# Revit family: 100800002 - Premier with base cabinets
name_source: partatom
category: Mechanical Equipment
units: mm (PartAtom-declared; Revit-internal decimal feet)

## family parameters
Always vertical = Yes
Cut with Voids When Loaded = No
Part Type = Normal
Room Calculation Point = No
Round Connector Dimension = Use Diameter
Shared = No
Work Plane-Based = No

## types (3) — shared parameters
Air Fixture = Plastic-Orange
Black iron piping = 0.375 "
Black iron piping for Gas = 0.375 "
CFM = 1180 CFM
Cold Water = Plastic-Orange
Collar = 10.53 "
Copper piping for Cold Water = 0.25 "
Cup Void Depth = 9 "
Cup Void Length 1 = 5.75 "
Exhaust Depth from Back = 9.3 "
Exterior Height = 59 "
Face Velocity = 100 FPM
Flange = Plastic-White
Fume Hood = Fume Hood
Height = 59 "
Interior Height = 48 "
Sash = Glass
Sash Seal = Sash Seal
Static Pressure Loss = 0.46 in-wg
URL = www.labconco.com
Work Surface Height = 1.25 "
zero-valued in all types: Default Elevation

## per-type parameters (varying)
| type | Cup Void Length 2 | Exhaust Distance (from Left Side) | Exterior Depth | Exterior Width | Gas | Interior Depth | Interior Width | Length / Total Width |
| XL 6' Width - 43.7" Depth | 52 " | 15 " | 43.7 " | 48 " | Plastic-Orange | 35.6 " | 62.25 " | 72 " |
| XL 6' Width - 37.7" Depth | 52 " | 15 " | 37.7 " | 48 " | Plastic-Orange | 29.6 " | 62.25 " | 72 " |
| XL 6' Width - 31.7" Depth | 40 " | 9 " | 31.7 " | 48.034 " | Plastic-Orange(1) | 23.6 " | 50.25 " | 60 " |

## geometry (parser evidence)
native form markers: Sweep x7
no freeform markers — native parametric forms only
